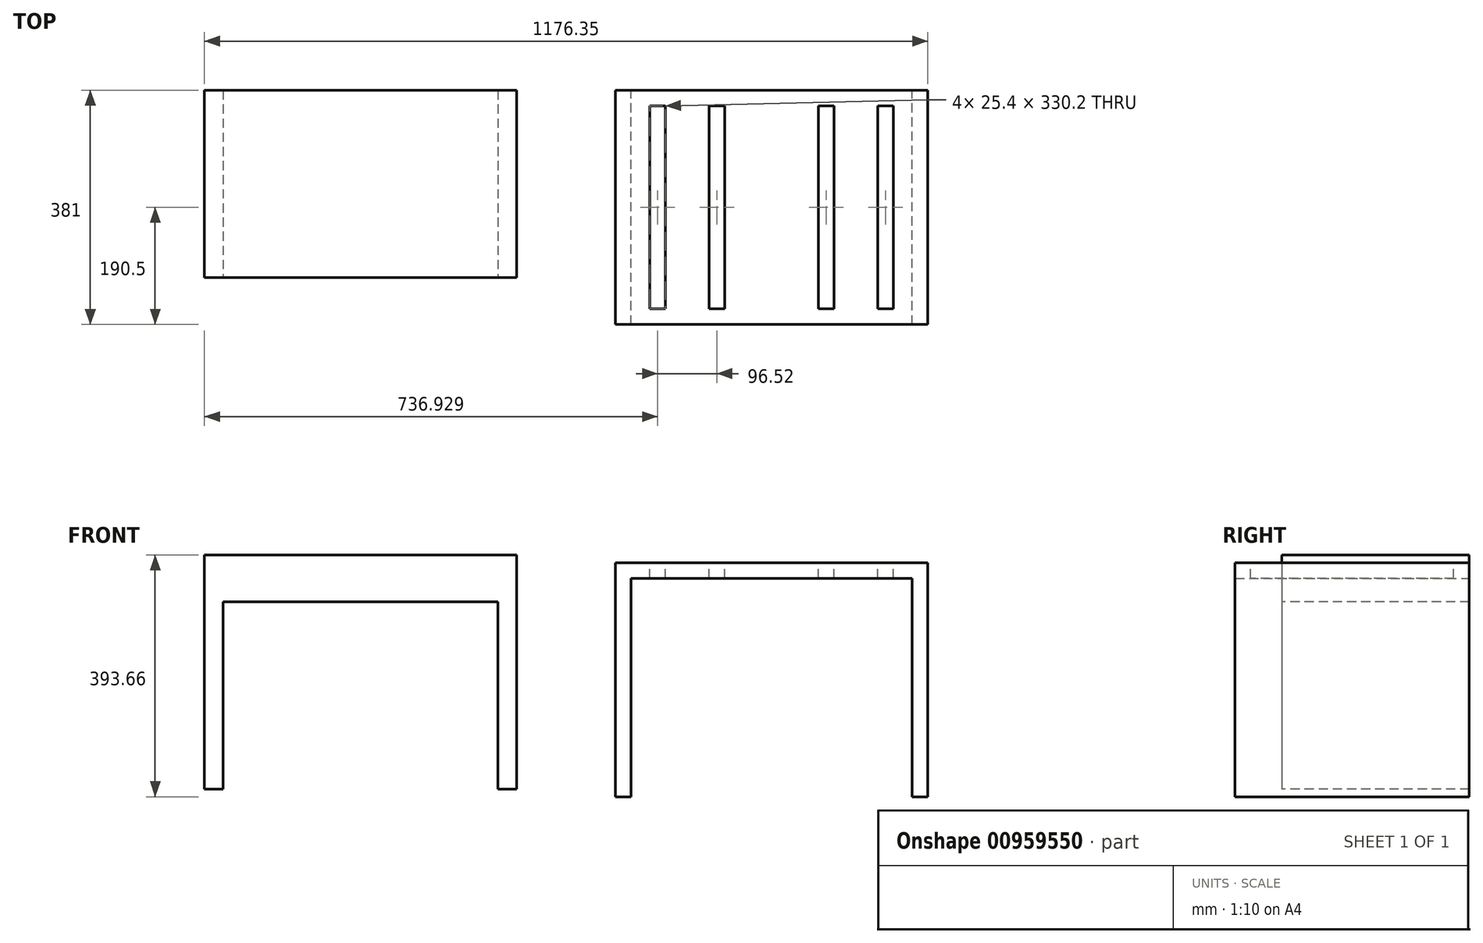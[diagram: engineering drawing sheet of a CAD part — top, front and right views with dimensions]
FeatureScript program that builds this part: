
annotation { "Feature Type Name" : "Feature", "Feature Type Description" : "" }
export const myFeature = defineFeature(function(context is Context, id is Id, definition is map)
    precondition{}
    {
        {
            var Q0;
            Q0=qCreatedBy(makeId("Front.planeOp"),FACE);
            var sketch = newSketch(context, id + "F0", { "sketchPlane" : qUnion([Q0])});
            skLineSegment(sketch, "E0.bottom", {"start": v(-299.23, 216.26) * mm, "end": v(208.77, 216.26) * mm});
            skLineSegment(sketch, "E0.top", {"start": v(-299.23, -164.74) * mm, "end": v(208.77, -164.74) * mm});
            skLineSegment(sketch, "E0.left", {"start": v(-299.23, 216.26) * mm, "end": v(-299.23, -164.74) * mm});
            skLineSegment(sketch, "E0.right", {"start": v(208.77, 216.26) * mm, "end": v(208.77, -164.74) * mm});
            skSolve(sketch);
        }
        {
            var Q0;
            Q0=makeQuery(id+"F0.imprint","IMPRINT",FACE,{"disambiguationData":[TD([[makeQuery(id+"F0.imprint","IMPRINT",EDGE,{"derivedFrom":sQuery(id+"F0.wireOp",EDGE,"E0.bottom")}),-1.0]])]});
            extrude(context, id + "F1", {"entities" : qUnion([Q0]), "depth" : 304.8 * mm, "offsetDistance" : 25.4 * mm});
        }
        {
            var Q0;
            Q0=makeQuery(id+"F1.opExtrude","CAP_FACE",FACE,{"disambiguationData":[OSD([sQuery(id+"F0.wireOp",EDGE,"E0.bottom"),sQuery(id+"F0.wireOp",EDGE,"E0.top"),sQuery(id+"F0.wireOp",EDGE,"E0.left"),sQuery(id+"F0.wireOp",EDGE,"E0.right")])],"isStart":false});
            var sketch = newSketch(context, id + "F2", { "sketchPlane" : qUnion([Q0])});
            skLineSegment(sketch, "E1.bottom", {"start": v(-268.75, 140.06) * mm, "end": v(178.29, 140.06) * mm});
            skLineSegment(sketch, "E1.top", {"start": v(-268.75, -164.74) * mm, "end": v(178.29, -164.74) * mm});
            skLineSegment(sketch, "E1.left", {"start": v(-268.75, 140.06) * mm, "end": v(-268.75, -164.74) * mm});
            skLineSegment(sketch, "E1.right", {"start": v(178.29, 140.06) * mm, "end": v(178.29, -164.74) * mm});
            skSolve(sketch);
        }
        {
            var Q0;
            Q0=makeQuery(id+"F2.imprint","IMPRINT",FACE,{"disambiguationData":[TD([[makeQuery(id+"F2.imprint","IMPRINT",EDGE,{"derivedFrom":sQuery(id+"F2.wireOp",EDGE,"E1.bottom")}),-1.0]])]});
            extrude(context, id + "F3", {"entities" : qUnion([Q0]), "operationType" : NewBodyOperationType.REMOVE, "oppositeDirection" : true, "depth" : 304.8 * mm, "offsetDistance" : 25.4 * mm});
        }
        {
            var Q0;
            Q0=qCreatedBy(makeId("Front.planeOp"),FACE);
            var sketch = newSketch(context, id + "F4", { "sketchPlane" : qUnion([Q0])});
            skLineSegment(sketch, "E2.bottom", {"start": v(369.12, 203.6) * mm, "end": v(877.12, 203.6) * mm});
            skLineSegment(sketch, "E2.top", {"start": v(369.12, -177.4) * mm, "end": v(877.12, -177.4) * mm});
            skLineSegment(sketch, "E2.left", {"start": v(369.12, 203.6) * mm, "end": v(369.12, -177.4) * mm});
            skLineSegment(sketch, "E2.right", {"start": v(877.12, 203.6) * mm, "end": v(877.12, -177.4) * mm});
            skSolve(sketch);
        }
        {
            var Q0;
            Q0=makeQuery(id+"F4.imprint","IMPRINT",FACE,{"disambiguationData":[TD([[makeQuery(id+"F4.imprint","IMPRINT",EDGE,{"derivedFrom":sQuery(id+"F4.wireOp",EDGE,"E2.bottom")}),-1.0]])]});
            extrude(context, id + "F5", {"entities" : qUnion([Q0]), "depth" : 381 * mm, "offsetDistance" : 25.4 * mm});
        }
        {
            var Q0;
            Q0=makeQuery(id+"F5.opExtrude","CAP_FACE",FACE,{"disambiguationData":[OSD([sQuery(id+"F4.wireOp",EDGE,"E2.bottom"),sQuery(id+"F4.wireOp",EDGE,"E2.top"),sQuery(id+"F4.wireOp",EDGE,"E2.left"),sQuery(id+"F4.wireOp",EDGE,"E2.right")])],"isStart":true});
            var sketch = newSketch(context, id + "F6", { "sketchPlane" : qUnion([Q0])});
            skLineSegment(sketch, "E3.bottom", {"start": v(-851.72, 178.2) * mm, "end": v(-394.52, 178.2) * mm});
            skLineSegment(sketch, "E3.top", {"start": v(-851.72, -177.4) * mm, "end": v(-394.52, -177.4) * mm});
            skLineSegment(sketch, "E3.left", {"start": v(-851.72, 178.2) * mm, "end": v(-851.72, -177.4) * mm});
            skLineSegment(sketch, "E3.right", {"start": v(-394.52, 178.2) * mm, "end": v(-394.52, -177.4) * mm});
            skSolve(sketch);
        }
        {
            var Q0;
            Q0=makeQuery(id+"F6.imprint","IMPRINT",FACE,{"disambiguationData":[TD([[makeQuery(id+"F6.imprint","IMPRINT",EDGE,{"derivedFrom":sQuery(id+"F6.wireOp",EDGE,"E3.bottom")}),-1.0]])]});
            extrude(context, id + "F7", {"entities" : qUnion([Q0]), "operationType" : NewBodyOperationType.REMOVE, "oppositeDirection" : true, "depth" : 381 * mm, "offsetDistance" : 25.4 * mm});
        }
        {
            var Q0;
            Q0=makeQuery(id+"F5.opExtrude","SWEPT_FACE",FACE,{"disambiguationData":[OSD([sQuery(id+"F4.wireOp",EDGE,"E2.bottom")])]});
            var sketch = newSketch(context, id + "F8", { "sketchPlane" : qUnion([Q0])});
            skLineSegment(sketch, "E4.bottom", {"start": v(425, -25.4) * mm, "end": v(450.4, -25.4) * mm});
            skLineSegment(sketch, "E4.top", {"start": v(425, -355.6) * mm, "end": v(450.4, -355.6) * mm});
            skLineSegment(sketch, "E5", {"start": v(425, -25.4) * mm, "end": v(425, -355.6) * mm});
            skLineSegment(sketch, "E6", {"start": v(450.4, -25.4) * mm, "end": v(450.4, -355.6) * mm});
            skLineSegment(sketch, "E7", {"start": v(821.24, -25.4) * mm, "end": v(821.24, -355.6) * mm});
            skLineSegment(sketch, "E8", {"start": v(795.84, -25.4) * mm, "end": v(795.84, -355.6) * mm});
            skLineSegment(sketch, "E9", {"start": v(521.52, -25.4) * mm, "end": v(521.52, -355.6) * mm});
            skLineSegment(sketch, "E10", {"start": v(546.92, -25.4) * mm, "end": v(546.92, -355.6) * mm});
            skLineSegment(sketch, "E11", {"start": v(699.32, -25.4) * mm, "end": v(699.32, -355.6) * mm});
            skLineSegment(sketch, "E12", {"start": v(724.72, -25.4) * mm, "end": v(724.72, -355.6) * mm});
            skLineSegment(sketch, "E13.trimOffspring", {"start": v(521.52, -25.4) * mm, "end": v(546.92, -25.4) * mm});
            skLineSegment(sketch, "E14.trimOffspring", {"start": v(795.84, -25.4) * mm, "end": v(821.24, -25.4) * mm});
            skLineSegment(sketch, "E15.trimOffspring", {"start": v(699.32, -25.4) * mm, "end": v(724.72, -25.4) * mm});
            skLineSegment(sketch, "E16.trimOffspring", {"start": v(521.52, -355.6) * mm, "end": v(546.92, -355.6) * mm});
            skLineSegment(sketch, "E17.trimOffspring", {"start": v(699.32, -355.6) * mm, "end": v(724.72, -355.6) * mm});
            skLineSegment(sketch, "E18.trimOffspring", {"start": v(795.84, -355.6) * mm, "end": v(821.24, -355.6) * mm});
            skSolve(sketch);
        }
        {
            var Q0;
            Q0=makeQuery(id+"F8.imprint","IMPRINT",FACE,{"disambiguationData":[TD([[makeQuery(id+"F8.imprint","IMPRINT",EDGE,{"derivedFrom":sQuery(id+"F8.wireOp",EDGE,"E4.bottom")}),-1.0]])]});
            var Q1;
            Q1=makeQuery(id+"F8.imprint","IMPRINT",FACE,{"disambiguationData":[TD([[makeQuery(id+"F8.imprint","IMPRINT",EDGE,{"derivedFrom":sQuery(id+"F8.wireOp",EDGE,"E9")}),1.0]])]});
            var Q2;
            Q2=makeQuery(id+"F8.imprint","IMPRINT",FACE,{"disambiguationData":[TD([[makeQuery(id+"F8.imprint","IMPRINT",EDGE,{"derivedFrom":sQuery(id+"F8.wireOp",EDGE,"E11")}),1.0]])]});
            var Q3;
            Q3=makeQuery(id+"F8.imprint","IMPRINT",FACE,{"disambiguationData":[TD([[makeQuery(id+"F8.imprint","IMPRINT",EDGE,{"derivedFrom":sQuery(id+"F8.wireOp",EDGE,"E7")}),-1.0]])]});
            extrude(context, id + "F9", {"entities" : qUnion([Q0, Q1, Q2, Q3]), "operationType" : NewBodyOperationType.REMOVE, "oppositeDirection" : true, "depth" : 25.4 * mm, "offsetDistance" : 25.4 * mm});
        }
    });
